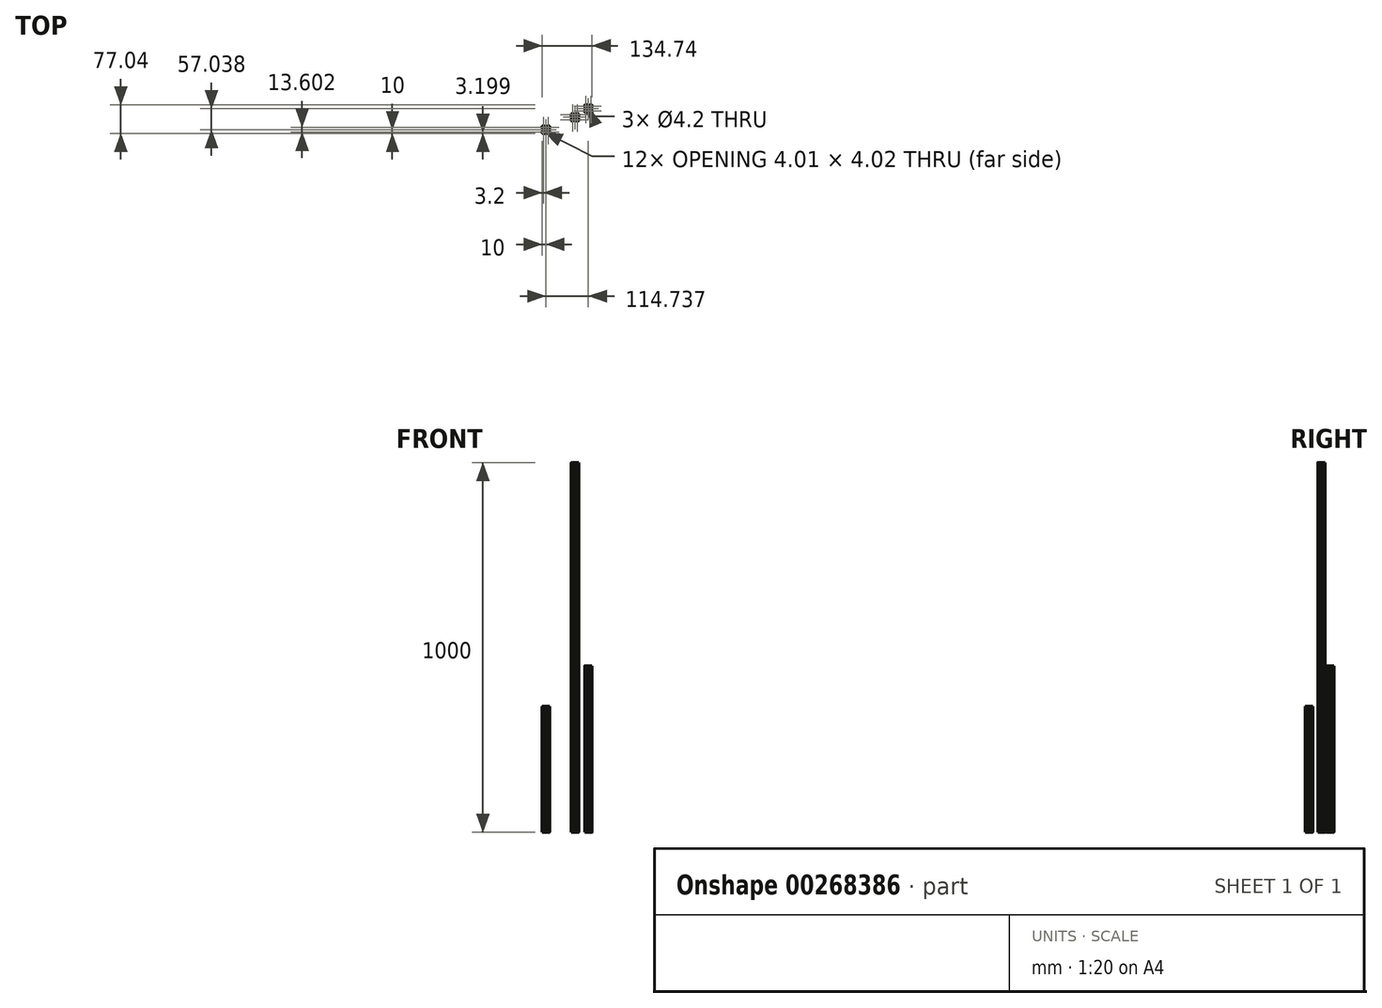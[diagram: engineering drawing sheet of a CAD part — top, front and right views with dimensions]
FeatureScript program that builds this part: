
annotation { "Feature Type Name" : "Feature", "Feature Type Description" : "" }
export const myFeature = defineFeature(function(context is Context, id is Id, definition is map)
    precondition{}
    {
        {
            var Q0;
            Q0=qCreatedBy(makeId("Top.planeOp"),FACE);
            var sketch = newSketch(context, id + "F0", { "sketchPlane" : qUnion([Q0])});
            skLineSegment(sketch, "E0", {"start": v(-9.77, 3.7) * mm, "end": v(-8.49, 2.4) * mm});
            skArc(sketch, "E1", {"start": v(-8.49, 2.4) * mm, "mid": v(-8.27, 2.36) * mm, "end": v(-8.14, 2.54) * mm});
            skLineSegment(sketch, "E2", {"start": v(-8.14, 2.54) * mm, "end": v(-8.14, 3.6) * mm});
            skLineSegment(sketch, "E3", {"start": v(-8.14, 3.6) * mm, "end": v(-5.03, 3.6) * mm});
            skLineSegment(sketch, "E4", {"start": v(-5.03, 3.6) * mm, "end": v(-3.4, 1.97) * mm});
            skLineSegment(sketch, "E5", {"start": v(-3.4, 1.97) * mm, "end": v(-3.4, 0.38) * mm});
            skLineSegment(sketch, "E6", {"start": v(-3.4, 0.38) * mm, "end": v(-3.02, 0) * mm});
            skLineSegment(sketch, "E7", {"start": v(-3.4, -0.38) * mm, "end": v(-3.02, 0) * mm});
            skLineSegment(sketch, "E8", {"start": v(-3.4, -1.97) * mm, "end": v(-3.4, -0.38) * mm});
            skLineSegment(sketch, "E9", {"start": v(-5.03, -3.6) * mm, "end": v(-3.4, -1.97) * mm});
            skLineSegment(sketch, "E10", {"start": v(-8.14, -3.6) * mm, "end": v(-5.03, -3.6) * mm});
            skLineSegment(sketch, "E11", {"start": v(-8.14, -2.54) * mm, "end": v(-8.14, -3.6) * mm});
            skArc(sketch, "E12", {"start": v(-8.49, -2.4) * mm, "mid": v(-8.27, -2.36) * mm, "end": v(-8.14, -2.54) * mm});
            skLineSegment(sketch, "E13", {"start": v(-9.77, -3.7) * mm, "end": v(-8.49, -2.4) * mm});
            skArc(sketch, "E14", {"start": v(-10, -4.25) * mm, "mid": v(-9.94, -3.95) * mm, "end": v(-9.77, -3.7) * mm});
            skLineSegment(sketch, "E15", {"start": v(-10, -8.58) * mm, "end": v(-10, -4.25) * mm});
            skArc(sketch, "E16", {"start": v(-8.6, -10) * mm, "mid": v(-9.57, -9.56) * mm, "end": v(-10, -8.58) * mm});
            skLineSegment(sketch, "E17", {"start": v(-4.04, -10) * mm, "end": v(-8.6, -10) * mm});
            skArc(sketch, "E18", {"start": v(-3.48, -9.77) * mm, "mid": v(-3.74, -9.94) * mm, "end": v(-4.04, -10) * mm});
            skLineSegment(sketch, "E19", {"start": v(-2.37, -8.66) * mm, "end": v(-3.48, -9.77) * mm});
            skArc(sketch, "E20", {"start": v(-2.55, -8.23) * mm, "mid": v(-2.32, -8.39) * mm, "end": v(-2.37, -8.66) * mm});
            skLineSegment(sketch, "E21", {"start": v(-3.6, -8.23) * mm, "end": v(-2.55, -8.23) * mm});
            skLineSegment(sketch, "E22", {"start": v(-3.6, -5.03) * mm, "end": v(-3.6, -8.23) * mm});
            skLineSegment(sketch, "E23", {"start": v(-2, -3.43) * mm, "end": v(-3.6, -5.03) * mm});
            skLineSegment(sketch, "E24", {"start": v(-0.3, -3.43) * mm, "end": v(-2, -3.43) * mm});
            skLineSegment(sketch, "E25", {"start": v(0, -3.18) * mm, "end": v(-0.3, -3.43) * mm});
            skLineSegment(sketch, "E26", {"start": v(0, -3.18) * mm, "end": v(0.3, -3.43) * mm});
            skLineSegment(sketch, "E27", {"start": v(0.3, -3.43) * mm, "end": v(2, -3.43) * mm});
            skLineSegment(sketch, "E28", {"start": v(2, -3.43) * mm, "end": v(3.6, -5.03) * mm});
            skLineSegment(sketch, "E29", {"start": v(3.6, -5.03) * mm, "end": v(3.6, -8.23) * mm});
            skLineSegment(sketch, "E30", {"start": v(3.6, -8.23) * mm, "end": v(2.55, -8.23) * mm});
            skArc(sketch, "E31", {"start": v(2.55, -8.23) * mm, "mid": v(2.32, -8.39) * mm, "end": v(2.37, -8.66) * mm});
            skLineSegment(sketch, "E32", {"start": v(2.37, -8.66) * mm, "end": v(3.48, -9.77) * mm});
            skArc(sketch, "E33", {"start": v(3.48, -9.77) * mm, "mid": v(3.74, -9.94) * mm, "end": v(4.04, -10) * mm});
            skLineSegment(sketch, "E34", {"start": v(4.04, -10) * mm, "end": v(8.6, -10) * mm});
            skArc(sketch, "E35", {"start": v(8.6, -10) * mm, "mid": v(9.57, -9.56) * mm, "end": v(10, -8.58) * mm});
            skLineSegment(sketch, "E36", {"start": v(10, -8.58) * mm, "end": v(10, -4.25) * mm});
            skArc(sketch, "E37", {"start": v(10, -4.25) * mm, "mid": v(9.94, -3.95) * mm, "end": v(9.77, -3.7) * mm});
            skLineSegment(sketch, "E38", {"start": v(9.77, -3.7) * mm, "end": v(8.49, -2.4) * mm});
            skArc(sketch, "E39", {"start": v(8.49, -2.4) * mm, "mid": v(8.27, -2.36) * mm, "end": v(8.14, -2.54) * mm});
            skLineSegment(sketch, "E40", {"start": v(8.14, -2.54) * mm, "end": v(8.14, -3.6) * mm});
            skLineSegment(sketch, "E41", {"start": v(8.14, -3.6) * mm, "end": v(5.03, -3.6) * mm});
            skLineSegment(sketch, "E42", {"start": v(5.03, -3.6) * mm, "end": v(3.4, -1.97) * mm});
            skLineSegment(sketch, "E43", {"start": v(3.4, -1.97) * mm, "end": v(3.4, -0.38) * mm});
            skLineSegment(sketch, "E44", {"start": v(3.4, -0.38) * mm, "end": v(3.02, 0) * mm});
            skLineSegment(sketch, "E45", {"start": v(3.4, 0.38) * mm, "end": v(3.02, 0) * mm});
            skLineSegment(sketch, "E46", {"start": v(3.4, 1.97) * mm, "end": v(3.4, 0.38) * mm});
            skLineSegment(sketch, "E47", {"start": v(5.03, 3.6) * mm, "end": v(3.4, 1.97) * mm});
            skLineSegment(sketch, "E48", {"start": v(8.14, 3.6) * mm, "end": v(5.03, 3.6) * mm});
            skLineSegment(sketch, "E49", {"start": v(8.14, 2.54) * mm, "end": v(8.14, 3.6) * mm});
            skArc(sketch, "E50", {"start": v(8.49, 2.4) * mm, "mid": v(8.27, 2.36) * mm, "end": v(8.14, 2.54) * mm});
            skLineSegment(sketch, "E51", {"start": v(9.77, 3.7) * mm, "end": v(8.49, 2.4) * mm});
            skArc(sketch, "E52", {"start": v(10, 4.25) * mm, "mid": v(9.94, 3.95) * mm, "end": v(9.77, 3.7) * mm});
            skLineSegment(sketch, "E53", {"start": v(10, 8.58) * mm, "end": v(10, 4.25) * mm});
            skArc(sketch, "E54", {"start": v(8.6, 10) * mm, "mid": v(9.57, 9.56) * mm, "end": v(10, 8.58) * mm});
            skLineSegment(sketch, "E55", {"start": v(4.04, 10) * mm, "end": v(8.6, 10) * mm});
            skArc(sketch, "E56", {"start": v(3.48, 9.77) * mm, "mid": v(3.74, 9.94) * mm, "end": v(4.04, 10) * mm});
            skLineSegment(sketch, "E57", {"start": v(2.37, 8.66) * mm, "end": v(3.48, 9.77) * mm});
            skArc(sketch, "E58", {"start": v(2.55, 8.23) * mm, "mid": v(2.32, 8.39) * mm, "end": v(2.37, 8.66) * mm});
            skLineSegment(sketch, "E59", {"start": v(3.6, 8.23) * mm, "end": v(2.55, 8.23) * mm});
            skLineSegment(sketch, "E60", {"start": v(3.6, 5.03) * mm, "end": v(3.6, 8.23) * mm});
            skLineSegment(sketch, "E61", {"start": v(2, 3.43) * mm, "end": v(3.6, 5.03) * mm});
            skLineSegment(sketch, "E62", {"start": v(0.3, 3.43) * mm, "end": v(2, 3.43) * mm});
            skLineSegment(sketch, "E63", {"start": v(0, 3.18) * mm, "end": v(0.3, 3.43) * mm});
            skLineSegment(sketch, "E64", {"start": v(0, 3.18) * mm, "end": v(-0.3, 3.43) * mm});
            skLineSegment(sketch, "E65", {"start": v(-0.3, 3.43) * mm, "end": v(-2, 3.43) * mm});
            skLineSegment(sketch, "E66", {"start": v(-2, 3.43) * mm, "end": v(-3.6, 5.03) * mm});
            skLineSegment(sketch, "E67", {"start": v(-3.6, 5.03) * mm, "end": v(-3.6, 8.23) * mm});
            skLineSegment(sketch, "E68", {"start": v(-3.6, 8.23) * mm, "end": v(-2.55, 8.23) * mm});
            skArc(sketch, "E69", {"start": v(-2.55, 8.23) * mm, "mid": v(-2.32, 8.39) * mm, "end": v(-2.37, 8.66) * mm});
            skLineSegment(sketch, "E70", {"start": v(-2.37, 8.66) * mm, "end": v(-3.48, 9.77) * mm});
            skArc(sketch, "E71", {"start": v(-3.48, 9.77) * mm, "mid": v(-3.74, 9.94) * mm, "end": v(-4.04, 10) * mm});
            skLineSegment(sketch, "E72", {"start": v(-4.04, 10) * mm, "end": v(-8.6, 10) * mm});
            skArc(sketch, "E73", {"start": v(-8.6, 10) * mm, "mid": v(-9.57, 9.56) * mm, "end": v(-10, 8.58) * mm});
            skLineSegment(sketch, "E74", {"start": v(-10, 8.58) * mm, "end": v(-10, 4.25) * mm});
            skArc(sketch, "E75", {"start": v(-10, 4.25) * mm, "mid": v(-9.94, 3.95) * mm, "end": v(-9.77, 3.7) * mm});
            skLineSegment(sketch, "E76", {"start": v(-8.8, -5.38) * mm, "end": v(-8.8, -8.38) * mm});
            skArc(sketch, "E77", {"start": v(-8.8, -5.38) * mm, "mid": v(-8.72, -5) * mm, "end": v(-8.39, -4.8) * mm});
            skLineSegment(sketch, "E78", {"start": v(-5.39, -4.8) * mm, "end": v(-8.39, -4.8) * mm});
            skArc(sketch, "E79", {"start": v(-5.39, -4.8) * mm, "mid": v(-4.94, -4.93) * mm, "end": v(-4.8, -5.38) * mm});
            skLineSegment(sketch, "E80", {"start": v(-4.8, -8.38) * mm, "end": v(-4.8, -5.38) * mm});
            skArc(sketch, "E81", {"start": v(-4.8, -8.38) * mm, "mid": v(-5, -8.72) * mm, "end": v(-5.4, -8.8) * mm});
            skLineSegment(sketch, "E82", {"start": v(-8.4, -8.8) * mm, "end": v(-5.4, -8.8) * mm});
            skArc(sketch, "E83", {"start": v(-8.4, -8.8) * mm, "mid": v(-8.67, -8.65) * mm, "end": v(-8.8, -8.38) * mm});
            skLineSegment(sketch, "E84", {"start": v(8.8, 5.38) * mm, "end": v(8.8, 8.38) * mm});
            skArc(sketch, "E85", {"start": v(8.8, 5.38) * mm, "mid": v(8.72, 5) * mm, "end": v(8.39, 4.8) * mm});
            skLineSegment(sketch, "E86", {"start": v(5.4, 4.93) * mm, "end": v(5.39, 4.8) * mm});
            skArc(sketch, "E87", {"start": v(5.39, 4.8) * mm, "mid": v(4.94, 4.93) * mm, "end": v(4.8, 5.38) * mm});
            skLineSegment(sketch, "E88", {"start": v(4.8, 8.38) * mm, "end": v(4.8, 5.38) * mm});
            skArc(sketch, "E89", {"start": v(4.8, 8.38) * mm, "mid": v(5, 8.72) * mm, "end": v(5.4, 8.8) * mm});
            skLineSegment(sketch, "E90", {"start": v(8.4, 8.8) * mm, "end": v(5.4, 8.8) * mm});
            skArc(sketch, "E91", {"start": v(8.4, 8.8) * mm, "mid": v(8.67, 8.65) * mm, "end": v(8.8, 8.38) * mm});
            skArc(sketch, "E92", {"start": v(5.39, -4.8) * mm, "mid": v(4.94, -4.93) * mm, "end": v(4.8, -5.38) * mm});
            skLineSegment(sketch, "E93", {"start": v(5.39, -4.8) * mm, "end": v(8.39, -4.8) * mm});
            skArc(sketch, "E94", {"start": v(8.8, -5.38) * mm, "mid": v(8.72, -5) * mm, "end": v(8.39, -4.8) * mm});
            skLineSegment(sketch, "E95", {"start": v(8.8, -5.38) * mm, "end": v(8.8, -8.38) * mm});
            skArc(sketch, "E96", {"start": v(8.4, -8.8) * mm, "mid": v(8.67, -8.65) * mm, "end": v(8.8, -8.38) * mm});
            skLineSegment(sketch, "E97", {"start": v(8.4, -8.8) * mm, "end": v(5.4, -8.8) * mm});
            skArc(sketch, "E98", {"start": v(4.8, -8.38) * mm, "mid": v(5, -8.72) * mm, "end": v(5.4, -8.8) * mm});
            skLineSegment(sketch, "E99", {"start": v(4.8, -8.38) * mm, "end": v(4.8, -5.38) * mm});
            skCircle(sketch, "E100", {"center": v(0, 0) * mm, "radius": 2.1 * mm});
            skArc(sketch, "E101", {"start": v(-5.39, 4.8) * mm, "mid": v(-4.94, 4.93) * mm, "end": v(-4.8, 5.38) * mm});
            skLineSegment(sketch, "E102", {"start": v(-5.39, 4.8) * mm, "end": v(-8.39, 4.8) * mm});
            skArc(sketch, "E103", {"start": v(-8.8, 5.38) * mm, "mid": v(-8.72, 5) * mm, "end": v(-8.39, 4.8) * mm});
            skLineSegment(sketch, "E104", {"start": v(-8.8, 5.38) * mm, "end": v(-8.8, 8.38) * mm});
            skArc(sketch, "E105", {"start": v(-8.4, 8.8) * mm, "mid": v(-8.67, 8.65) * mm, "end": v(-8.8, 8.38) * mm});
            skLineSegment(sketch, "E106", {"start": v(-8.4, 8.8) * mm, "end": v(-5.4, 8.8) * mm});
            skArc(sketch, "E107", {"start": v(-4.8, 8.38) * mm, "mid": v(-5, 8.72) * mm, "end": v(-5.4, 8.8) * mm});
            skLineSegment(sketch, "E108", {"start": v(-4.8, 8.38) * mm, "end": v(-4.8, 5.38) * mm});
            skLineSegment(sketch, "E109", {"start": v(5.39, 4.8) * mm, "end": v(8.39, 4.8) * mm});
            skLineSegment(sketch, "E110", {"start": v(-0.3, -3.43) * mm, "end": v(0.56, -10) * mm, "construction": true});
            skLineSegment(sketch, "E111", {"start": v(104.97, 60.73) * mm, "end": v(106.25, 59.45) * mm});
            skArc(sketch, "E112", {"start": v(106.25, 59.45) * mm, "mid": v(106.46, 59.4) * mm, "end": v(106.6, 59.58) * mm});
            skLineSegment(sketch, "E113", {"start": v(106.6, 59.58) * mm, "end": v(106.6, 60.64) * mm});
            skLineSegment(sketch, "E114", {"start": v(106.6, 60.64) * mm, "end": v(109.7, 60.64) * mm});
            skLineSegment(sketch, "E115", {"start": v(109.7, 60.64) * mm, "end": v(111.34, 59) * mm});
            skLineSegment(sketch, "E116", {"start": v(111.34, 59) * mm, "end": v(111.34, 57.42) * mm});
            skLineSegment(sketch, "E117", {"start": v(111.34, 57.42) * mm, "end": v(111.72, 57.04) * mm});
            skLineSegment(sketch, "E118", {"start": v(111.34, 56.66) * mm, "end": v(111.72, 57.04) * mm});
            skLineSegment(sketch, "E119", {"start": v(111.34, 55.07) * mm, "end": v(111.34, 56.66) * mm});
            skLineSegment(sketch, "E120", {"start": v(109.7, 53.44) * mm, "end": v(111.34, 55.07) * mm});
            skLineSegment(sketch, "E121", {"start": v(106.6, 53.44) * mm, "end": v(109.7, 53.44) * mm});
            skLineSegment(sketch, "E122", {"start": v(106.6, 54.5) * mm, "end": v(106.6, 53.44) * mm});
            skArc(sketch, "E123", {"start": v(106.25, 54.63) * mm, "mid": v(106.46, 54.67) * mm, "end": v(106.6, 54.5) * mm});
            skLineSegment(sketch, "E124", {"start": v(104.97, 53.35) * mm, "end": v(106.25, 54.63) * mm});
            skArc(sketch, "E125", {"start": v(104.74, 52.79) * mm, "mid": v(104.8, 53.1) * mm, "end": v(104.97, 53.35) * mm});
            skLineSegment(sketch, "E126", {"start": v(104.74, 48.46) * mm, "end": v(104.74, 52.79) * mm});
            skArc(sketch, "E127", {"start": v(106.14, 47.04) * mm, "mid": v(105.17, 47.48) * mm, "end": v(104.74, 48.46) * mm});
            skLineSegment(sketch, "E128", {"start": v(110.7, 47.04) * mm, "end": v(106.14, 47.04) * mm});
            skArc(sketch, "E129", {"start": v(111.26, 47.27) * mm, "mid": v(111, 47.1) * mm, "end": v(110.7, 47.04) * mm});
            skLineSegment(sketch, "E130", {"start": v(112.36, 48.38) * mm, "end": v(111.26, 47.27) * mm});
            skArc(sketch, "E131", {"start": v(112.19, 48.8) * mm, "mid": v(112.42, 48.65) * mm, "end": v(112.36, 48.38) * mm});
            skLineSegment(sketch, "E132", {"start": v(111.14, 48.8) * mm, "end": v(112.19, 48.8) * mm});
            skLineSegment(sketch, "E133", {"start": v(111.14, 52) * mm, "end": v(111.14, 48.8) * mm});
            skLineSegment(sketch, "E134", {"start": v(112.73, 53.6) * mm, "end": v(111.14, 52) * mm});
            skLineSegment(sketch, "E135", {"start": v(114.44, 53.6) * mm, "end": v(112.73, 53.6) * mm});
            skLineSegment(sketch, "E136", {"start": v(114.74, 53.86) * mm, "end": v(114.44, 53.6) * mm});
            skLineSegment(sketch, "E137", {"start": v(114.74, 53.86) * mm, "end": v(115.04, 53.6) * mm});
            skLineSegment(sketch, "E138", {"start": v(115.04, 53.6) * mm, "end": v(116.74, 53.6) * mm});
            skLineSegment(sketch, "E139", {"start": v(116.74, 53.6) * mm, "end": v(118.34, 52) * mm});
            skLineSegment(sketch, "E140", {"start": v(118.34, 52) * mm, "end": v(118.34, 48.8) * mm});
            skLineSegment(sketch, "E141", {"start": v(118.34, 48.8) * mm, "end": v(117.29, 48.8) * mm});
            skArc(sketch, "E142", {"start": v(117.29, 48.8) * mm, "mid": v(117.06, 48.65) * mm, "end": v(117.11, 48.38) * mm});
            skLineSegment(sketch, "E143", {"start": v(117.11, 48.38) * mm, "end": v(118.21, 47.27) * mm});
            skArc(sketch, "E144", {"start": v(118.21, 47.27) * mm, "mid": v(118.47, 47.1) * mm, "end": v(118.78, 47.04) * mm});
            skLineSegment(sketch, "E145", {"start": v(118.78, 47.04) * mm, "end": v(123.34, 47.04) * mm});
            skArc(sketch, "E146", {"start": v(123.34, 47.04) * mm, "mid": v(124.3, 47.48) * mm, "end": v(124.74, 48.46) * mm});
            skLineSegment(sketch, "E147", {"start": v(124.74, 48.46) * mm, "end": v(124.74, 52.79) * mm});
            skArc(sketch, "E148", {"start": v(124.74, 52.79) * mm, "mid": v(124.68, 53.1) * mm, "end": v(124.5, 53.35) * mm});
            skLineSegment(sketch, "E149", {"start": v(124.5, 53.35) * mm, "end": v(123.22, 54.63) * mm});
            skArc(sketch, "E150", {"start": v(123.22, 54.63) * mm, "mid": v(123, 54.67) * mm, "end": v(122.88, 54.5) * mm});
            skLineSegment(sketch, "E151", {"start": v(122.88, 54.5) * mm, "end": v(122.88, 53.44) * mm});
            skLineSegment(sketch, "E152", {"start": v(122.88, 53.44) * mm, "end": v(119.77, 53.44) * mm});
            skLineSegment(sketch, "E153", {"start": v(119.77, 53.44) * mm, "end": v(118.14, 55.07) * mm});
            skLineSegment(sketch, "E154", {"start": v(118.14, 55.07) * mm, "end": v(118.14, 56.66) * mm});
            skLineSegment(sketch, "E155", {"start": v(118.14, 56.66) * mm, "end": v(117.76, 57.04) * mm});
            skLineSegment(sketch, "E156", {"start": v(118.14, 57.42) * mm, "end": v(117.76, 57.04) * mm});
            skLineSegment(sketch, "E157", {"start": v(118.14, 59) * mm, "end": v(118.14, 57.42) * mm});
            skLineSegment(sketch, "E158", {"start": v(119.77, 60.64) * mm, "end": v(118.14, 59) * mm});
            skLineSegment(sketch, "E159", {"start": v(122.88, 60.64) * mm, "end": v(119.77, 60.64) * mm});
            skLineSegment(sketch, "E160", {"start": v(122.88, 59.58) * mm, "end": v(122.88, 60.64) * mm});
            skArc(sketch, "E161", {"start": v(123.22, 59.45) * mm, "mid": v(123, 59.4) * mm, "end": v(122.88, 59.58) * mm});
            skLineSegment(sketch, "E162", {"start": v(124.5, 60.73) * mm, "end": v(123.22, 59.45) * mm});
            skArc(sketch, "E163", {"start": v(124.74, 61.29) * mm, "mid": v(124.68, 60.98) * mm, "end": v(124.5, 60.73) * mm});
            skLineSegment(sketch, "E164", {"start": v(124.74, 65.62) * mm, "end": v(124.74, 61.29) * mm});
            skArc(sketch, "E165", {"start": v(123.34, 67.04) * mm, "mid": v(124.3, 66.6) * mm, "end": v(124.74, 65.62) * mm});
            skLineSegment(sketch, "E166", {"start": v(118.78, 67.04) * mm, "end": v(123.34, 67.04) * mm});
            skArc(sketch, "E167", {"start": v(118.21, 66.8) * mm, "mid": v(118.47, 66.98) * mm, "end": v(118.78, 67.04) * mm});
            skLineSegment(sketch, "E168", {"start": v(117.11, 65.7) * mm, "end": v(118.21, 66.8) * mm});
            skArc(sketch, "E169", {"start": v(117.29, 65.27) * mm, "mid": v(117.06, 65.43) * mm, "end": v(117.11, 65.7) * mm});
            skLineSegment(sketch, "E170", {"start": v(118.34, 65.27) * mm, "end": v(117.29, 65.27) * mm});
            skLineSegment(sketch, "E171", {"start": v(118.34, 62.07) * mm, "end": v(118.34, 65.27) * mm});
            skLineSegment(sketch, "E172", {"start": v(116.74, 60.47) * mm, "end": v(118.34, 62.07) * mm});
            skLineSegment(sketch, "E173", {"start": v(115.04, 60.47) * mm, "end": v(116.74, 60.47) * mm});
            skLineSegment(sketch, "E174", {"start": v(114.74, 60.21) * mm, "end": v(115.04, 60.47) * mm});
            skLineSegment(sketch, "E175", {"start": v(114.74, 60.21) * mm, "end": v(114.44, 60.47) * mm});
            skLineSegment(sketch, "E176", {"start": v(114.44, 60.47) * mm, "end": v(112.73, 60.47) * mm});
            skLineSegment(sketch, "E177", {"start": v(112.73, 60.47) * mm, "end": v(111.14, 62.07) * mm});
            skLineSegment(sketch, "E178", {"start": v(111.14, 62.07) * mm, "end": v(111.14, 65.27) * mm});
            skLineSegment(sketch, "E179", {"start": v(111.14, 65.27) * mm, "end": v(112.19, 65.27) * mm});
            skArc(sketch, "E180", {"start": v(112.19, 65.27) * mm, "mid": v(112.42, 65.43) * mm, "end": v(112.36, 65.7) * mm});
            skLineSegment(sketch, "E181", {"start": v(112.36, 65.7) * mm, "end": v(111.26, 66.8) * mm});
            skArc(sketch, "E182", {"start": v(111.26, 66.8) * mm, "mid": v(111, 66.98) * mm, "end": v(110.7, 67.04) * mm});
            skLineSegment(sketch, "E183", {"start": v(110.7, 67.04) * mm, "end": v(106.14, 67.04) * mm});
            skArc(sketch, "E184", {"start": v(106.14, 67.04) * mm, "mid": v(105.17, 66.6) * mm, "end": v(104.74, 65.62) * mm});
            skLineSegment(sketch, "E185", {"start": v(104.74, 65.62) * mm, "end": v(104.74, 61.29) * mm});
            skArc(sketch, "E186", {"start": v(104.74, 61.29) * mm, "mid": v(104.8, 60.98) * mm, "end": v(104.97, 60.73) * mm});
            skLineSegment(sketch, "E187", {"start": v(105.94, 51.66) * mm, "end": v(105.94, 48.66) * mm});
            skArc(sketch, "E188", {"start": v(105.94, 51.66) * mm, "mid": v(106.02, 52.03) * mm, "end": v(106.35, 52.24) * mm});
            skLineSegment(sketch, "E189", {"start": v(109.35, 52.24) * mm, "end": v(106.35, 52.24) * mm});
            skArc(sketch, "E190", {"start": v(109.35, 52.24) * mm, "mid": v(109.8, 52.1) * mm, "end": v(109.94, 51.66) * mm});
            skLineSegment(sketch, "E191", {"start": v(109.94, 48.66) * mm, "end": v(109.94, 51.66) * mm});
            skArc(sketch, "E192", {"start": v(109.94, 48.66) * mm, "mid": v(109.73, 48.32) * mm, "end": v(109.34, 48.24) * mm});
            skLineSegment(sketch, "E193", {"start": v(106.34, 48.24) * mm, "end": v(109.34, 48.24) * mm});
            skArc(sketch, "E194", {"start": v(106.34, 48.24) * mm, "mid": v(106.07, 48.38) * mm, "end": v(105.94, 48.66) * mm});
            skLineSegment(sketch, "E195", {"start": v(123.54, 62.42) * mm, "end": v(123.54, 65.42) * mm});
            skArc(sketch, "E196", {"start": v(123.54, 62.42) * mm, "mid": v(123.45, 62.04) * mm, "end": v(123.13, 61.84) * mm});
            skLineSegment(sketch, "E197", {"start": v(120.13, 61.97) * mm, "end": v(120.13, 61.84) * mm});
            skArc(sketch, "E198", {"start": v(120.13, 61.84) * mm, "mid": v(119.68, 61.97) * mm, "end": v(119.54, 62.42) * mm});
            skLineSegment(sketch, "E199", {"start": v(119.54, 65.42) * mm, "end": v(119.54, 62.42) * mm});
            skArc(sketch, "E200", {"start": v(119.54, 65.42) * mm, "mid": v(119.75, 65.76) * mm, "end": v(120.14, 65.84) * mm});
            skLineSegment(sketch, "E201", {"start": v(123.14, 65.84) * mm, "end": v(120.14, 65.84) * mm});
            skArc(sketch, "E202", {"start": v(123.14, 65.84) * mm, "mid": v(123.4, 65.7) * mm, "end": v(123.54, 65.42) * mm});
            skArc(sketch, "E203", {"start": v(120.13, 52.24) * mm, "mid": v(119.68, 52.1) * mm, "end": v(119.54, 51.66) * mm});
            skLineSegment(sketch, "E204", {"start": v(120.13, 52.24) * mm, "end": v(123.13, 52.24) * mm});
            skArc(sketch, "E205", {"start": v(123.54, 51.66) * mm, "mid": v(123.45, 52.03) * mm, "end": v(123.13, 52.24) * mm});
            skLineSegment(sketch, "E206", {"start": v(123.54, 51.66) * mm, "end": v(123.54, 48.66) * mm});
            skArc(sketch, "E207", {"start": v(123.14, 48.24) * mm, "mid": v(123.4, 48.38) * mm, "end": v(123.54, 48.66) * mm});
            skLineSegment(sketch, "E208", {"start": v(123.14, 48.24) * mm, "end": v(120.14, 48.24) * mm});
            skArc(sketch, "E209", {"start": v(119.54, 48.66) * mm, "mid": v(119.75, 48.32) * mm, "end": v(120.14, 48.24) * mm});
            skLineSegment(sketch, "E210", {"start": v(119.54, 48.66) * mm, "end": v(119.54, 51.66) * mm});
            skCircle(sketch, "E211", {"center": v(114.74, 57.04) * mm, "radius": 2.1 * mm});
            skArc(sketch, "E212", {"start": v(109.35, 61.84) * mm, "mid": v(109.8, 61.97) * mm, "end": v(109.94, 62.42) * mm});
            skLineSegment(sketch, "E213", {"start": v(109.35, 61.84) * mm, "end": v(106.35, 61.84) * mm});
            skArc(sketch, "E214", {"start": v(105.94, 62.42) * mm, "mid": v(106.02, 62.04) * mm, "end": v(106.35, 61.84) * mm});
            skLineSegment(sketch, "E215", {"start": v(105.94, 62.42) * mm, "end": v(105.94, 65.42) * mm});
            skArc(sketch, "E216", {"start": v(106.34, 65.84) * mm, "mid": v(106.07, 65.7) * mm, "end": v(105.94, 65.42) * mm});
            skLineSegment(sketch, "E217", {"start": v(106.34, 65.84) * mm, "end": v(109.34, 65.84) * mm});
            skArc(sketch, "E218", {"start": v(109.94, 65.42) * mm, "mid": v(109.73, 65.76) * mm, "end": v(109.34, 65.84) * mm});
            skLineSegment(sketch, "E219", {"start": v(109.94, 65.42) * mm, "end": v(109.94, 62.42) * mm});
            skLineSegment(sketch, "E220", {"start": v(120.13, 61.84) * mm, "end": v(123.13, 61.84) * mm});
            skLineSegment(sketch, "E221", {"start": v(114.44, 53.6) * mm, "end": v(115.3, 47.04) * mm, "construction": true});
            skLineSegment(sketch, "E222", {"start": v(68.81, 37.37) * mm, "end": v(70.1, 36.09) * mm});
            skArc(sketch, "E223", {"start": v(70.1, 36.09) * mm, "mid": v(70.3, 36.04) * mm, "end": v(70.44, 36.22) * mm});
            skLineSegment(sketch, "E224", {"start": v(70.44, 36.22) * mm, "end": v(70.44, 37.28) * mm});
            skLineSegment(sketch, "E225", {"start": v(70.44, 37.28) * mm, "end": v(73.55, 37.28) * mm});
            skLineSegment(sketch, "E226", {"start": v(73.55, 37.28) * mm, "end": v(75.18, 35.65) * mm});
            skLineSegment(sketch, "E227", {"start": v(75.18, 35.65) * mm, "end": v(75.18, 34.06) * mm});
            skLineSegment(sketch, "E228", {"start": v(75.18, 34.06) * mm, "end": v(75.56, 33.68) * mm});
            skLineSegment(sketch, "E229", {"start": v(75.18, 33.3) * mm, "end": v(75.56, 33.68) * mm});
            skLineSegment(sketch, "E230", {"start": v(75.18, 31.71) * mm, "end": v(75.18, 33.3) * mm});
            skLineSegment(sketch, "E231", {"start": v(73.55, 30.08) * mm, "end": v(75.18, 31.71) * mm});
            skLineSegment(sketch, "E232", {"start": v(70.44, 30.08) * mm, "end": v(73.55, 30.08) * mm});
            skLineSegment(sketch, "E233", {"start": v(70.44, 31.14) * mm, "end": v(70.44, 30.08) * mm});
            skArc(sketch, "E234", {"start": v(70.1, 31.27) * mm, "mid": v(70.3, 31.32) * mm, "end": v(70.44, 31.14) * mm});
            skLineSegment(sketch, "E235", {"start": v(68.81, 29.99) * mm, "end": v(70.1, 31.27) * mm});
            skArc(sketch, "E236", {"start": v(68.58, 29.43) * mm, "mid": v(68.64, 29.73) * mm, "end": v(68.81, 29.99) * mm});
            skLineSegment(sketch, "E237", {"start": v(68.58, 25.1) * mm, "end": v(68.58, 29.43) * mm});
            skArc(sketch, "E238", {"start": v(69.98, 23.68) * mm, "mid": v(69.01, 24.12) * mm, "end": v(68.58, 25.1) * mm});
            skLineSegment(sketch, "E239", {"start": v(74.54, 23.68) * mm, "end": v(69.98, 23.68) * mm});
            skArc(sketch, "E240", {"start": v(75.1, 23.91) * mm, "mid": v(74.84, 23.74) * mm, "end": v(74.54, 23.68) * mm});
            skLineSegment(sketch, "E241", {"start": v(76.2, 25.02) * mm, "end": v(75.1, 23.91) * mm});
            skArc(sketch, "E242", {"start": v(76.03, 25.44) * mm, "mid": v(76.26, 25.29) * mm, "end": v(76.2, 25.02) * mm});
            skLineSegment(sketch, "E243", {"start": v(74.98, 25.44) * mm, "end": v(76.03, 25.44) * mm});
            skLineSegment(sketch, "E244", {"start": v(74.98, 28.64) * mm, "end": v(74.98, 25.44) * mm});
            skLineSegment(sketch, "E245", {"start": v(76.57, 30.24) * mm, "end": v(74.98, 28.64) * mm});
            skLineSegment(sketch, "E246", {"start": v(78.28, 30.24) * mm, "end": v(76.57, 30.24) * mm});
            skLineSegment(sketch, "E247", {"start": v(78.58, 30.5) * mm, "end": v(78.28, 30.24) * mm});
            skLineSegment(sketch, "E248", {"start": v(78.58, 30.5) * mm, "end": v(78.88, 30.24) * mm});
            skLineSegment(sketch, "E249", {"start": v(78.88, 30.24) * mm, "end": v(80.59, 30.24) * mm});
            skLineSegment(sketch, "E250", {"start": v(80.59, 30.24) * mm, "end": v(82.18, 28.64) * mm});
            skLineSegment(sketch, "E251", {"start": v(82.18, 28.64) * mm, "end": v(82.18, 25.44) * mm});
            skLineSegment(sketch, "E252", {"start": v(82.18, 25.44) * mm, "end": v(81.13, 25.44) * mm});
            skArc(sketch, "E253", {"start": v(81.13, 25.44) * mm, "mid": v(80.9, 25.29) * mm, "end": v(80.95, 25.02) * mm});
            skLineSegment(sketch, "E254", {"start": v(80.95, 25.02) * mm, "end": v(82.06, 23.91) * mm});
            skArc(sketch, "E255", {"start": v(82.06, 23.91) * mm, "mid": v(82.32, 23.74) * mm, "end": v(82.62, 23.68) * mm});
            skLineSegment(sketch, "E256", {"start": v(82.62, 23.68) * mm, "end": v(87.18, 23.68) * mm});
            skArc(sketch, "E257", {"start": v(87.18, 23.68) * mm, "mid": v(88.15, 24.12) * mm, "end": v(88.58, 25.1) * mm});
            skLineSegment(sketch, "E258", {"start": v(88.58, 25.1) * mm, "end": v(88.58, 29.43) * mm});
            skArc(sketch, "E259", {"start": v(88.58, 29.43) * mm, "mid": v(88.52, 29.73) * mm, "end": v(88.35, 29.99) * mm});
            skLineSegment(sketch, "E260", {"start": v(88.35, 29.99) * mm, "end": v(87.07, 31.27) * mm});
            skArc(sketch, "E261", {"start": v(87.07, 31.27) * mm, "mid": v(86.85, 31.32) * mm, "end": v(86.73, 31.14) * mm});
            skLineSegment(sketch, "E262", {"start": v(86.73, 31.14) * mm, "end": v(86.73, 30.08) * mm});
            skLineSegment(sketch, "E263", {"start": v(86.73, 30.08) * mm, "end": v(83.6, 30.08) * mm});
            skLineSegment(sketch, "E264", {"start": v(83.6, 30.08) * mm, "end": v(81.98, 31.71) * mm});
            skLineSegment(sketch, "E265", {"start": v(81.98, 31.71) * mm, "end": v(81.98, 33.3) * mm});
            skLineSegment(sketch, "E266", {"start": v(81.98, 33.3) * mm, "end": v(81.6, 33.68) * mm});
            skLineSegment(sketch, "E267", {"start": v(81.98, 34.06) * mm, "end": v(81.6, 33.68) * mm});
            skLineSegment(sketch, "E268", {"start": v(81.98, 35.65) * mm, "end": v(81.98, 34.06) * mm});
            skLineSegment(sketch, "E269", {"start": v(83.6, 37.28) * mm, "end": v(81.98, 35.65) * mm});
            skLineSegment(sketch, "E270", {"start": v(86.73, 37.28) * mm, "end": v(83.6, 37.28) * mm});
            skLineSegment(sketch, "E271", {"start": v(86.73, 36.22) * mm, "end": v(86.73, 37.28) * mm});
            skArc(sketch, "E272", {"start": v(87.07, 36.09) * mm, "mid": v(86.85, 36.04) * mm, "end": v(86.73, 36.22) * mm});
            skLineSegment(sketch, "E273", {"start": v(88.35, 37.37) * mm, "end": v(87.07, 36.09) * mm});
            skArc(sketch, "E274", {"start": v(88.58, 37.93) * mm, "mid": v(88.52, 37.63) * mm, "end": v(88.35, 37.37) * mm});
            skLineSegment(sketch, "E275", {"start": v(88.58, 42.26) * mm, "end": v(88.58, 37.93) * mm});
            skArc(sketch, "E276", {"start": v(87.18, 43.68) * mm, "mid": v(88.15, 43.24) * mm, "end": v(88.58, 42.26) * mm});
            skLineSegment(sketch, "E277", {"start": v(82.62, 43.68) * mm, "end": v(87.18, 43.68) * mm});
            skArc(sketch, "E278", {"start": v(82.06, 43.44) * mm, "mid": v(82.32, 43.62) * mm, "end": v(82.62, 43.68) * mm});
            skLineSegment(sketch, "E279", {"start": v(80.95, 42.34) * mm, "end": v(82.06, 43.44) * mm});
            skArc(sketch, "E280", {"start": v(81.13, 41.91) * mm, "mid": v(80.9, 42.07) * mm, "end": v(80.95, 42.34) * mm});
            skLineSegment(sketch, "E281", {"start": v(82.18, 41.91) * mm, "end": v(81.13, 41.91) * mm});
            skLineSegment(sketch, "E282", {"start": v(82.18, 38.71) * mm, "end": v(82.18, 41.91) * mm});
            skLineSegment(sketch, "E283", {"start": v(80.59, 37.11) * mm, "end": v(82.18, 38.71) * mm});
            skLineSegment(sketch, "E284", {"start": v(78.88, 37.11) * mm, "end": v(80.59, 37.11) * mm});
            skLineSegment(sketch, "E285", {"start": v(78.58, 36.85) * mm, "end": v(78.88, 37.11) * mm});
            skLineSegment(sketch, "E286", {"start": v(78.58, 36.85) * mm, "end": v(78.28, 37.11) * mm});
            skLineSegment(sketch, "E287", {"start": v(78.28, 37.11) * mm, "end": v(76.57, 37.11) * mm});
            skLineSegment(sketch, "E288", {"start": v(76.57, 37.11) * mm, "end": v(74.98, 38.71) * mm});
            skLineSegment(sketch, "E289", {"start": v(74.98, 38.71) * mm, "end": v(74.98, 41.91) * mm});
            skLineSegment(sketch, "E290", {"start": v(74.98, 41.91) * mm, "end": v(76.03, 41.91) * mm});
            skArc(sketch, "E291", {"start": v(76.03, 41.91) * mm, "mid": v(76.26, 42.07) * mm, "end": v(76.2, 42.34) * mm});
            skLineSegment(sketch, "E292", {"start": v(76.2, 42.34) * mm, "end": v(75.1, 43.44) * mm});
            skArc(sketch, "E293", {"start": v(75.1, 43.44) * mm, "mid": v(74.84, 43.62) * mm, "end": v(74.54, 43.68) * mm});
            skLineSegment(sketch, "E294", {"start": v(74.54, 43.68) * mm, "end": v(69.98, 43.68) * mm});
            skArc(sketch, "E295", {"start": v(69.98, 43.68) * mm, "mid": v(69.01, 43.24) * mm, "end": v(68.58, 42.26) * mm});
            skLineSegment(sketch, "E296", {"start": v(68.58, 42.26) * mm, "end": v(68.58, 37.93) * mm});
            skArc(sketch, "E297", {"start": v(68.58, 37.93) * mm, "mid": v(68.64, 37.63) * mm, "end": v(68.81, 37.37) * mm});
            skLineSegment(sketch, "E298", {"start": v(69.78, 28.3) * mm, "end": v(69.78, 25.3) * mm});
            skArc(sketch, "E299", {"start": v(69.78, 28.3) * mm, "mid": v(69.86, 28.67) * mm, "end": v(70.2, 28.88) * mm});
            skLineSegment(sketch, "E300", {"start": v(73.2, 28.88) * mm, "end": v(70.2, 28.88) * mm});
            skArc(sketch, "E301", {"start": v(73.2, 28.88) * mm, "mid": v(73.64, 28.74) * mm, "end": v(73.78, 28.3) * mm});
            skLineSegment(sketch, "E302", {"start": v(73.78, 25.3) * mm, "end": v(73.78, 28.3) * mm});
            skArc(sketch, "E303", {"start": v(73.78, 25.3) * mm, "mid": v(73.57, 24.96) * mm, "end": v(73.18, 24.88) * mm});
            skLineSegment(sketch, "E304", {"start": v(70.18, 24.88) * mm, "end": v(73.18, 24.88) * mm});
            skArc(sketch, "E305", {"start": v(70.18, 24.88) * mm, "mid": v(69.91, 25.02) * mm, "end": v(69.78, 25.3) * mm});
            skLineSegment(sketch, "E306", {"start": v(87.38, 39.06) * mm, "end": v(87.38, 42.06) * mm});
            skArc(sketch, "E307", {"start": v(87.38, 39.06) * mm, "mid": v(87.3, 38.68) * mm, "end": v(86.97, 38.48) * mm});
            skLineSegment(sketch, "E308", {"start": v(83.97, 38.6) * mm, "end": v(83.97, 38.48) * mm});
            skArc(sketch, "E309", {"start": v(83.97, 38.48) * mm, "mid": v(83.52, 38.61) * mm, "end": v(83.38, 39.06) * mm});
            skLineSegment(sketch, "E310", {"start": v(83.38, 42.06) * mm, "end": v(83.38, 39.06) * mm});
            skArc(sketch, "E311", {"start": v(83.38, 42.06) * mm, "mid": v(83.59, 42.4) * mm, "end": v(83.98, 42.48) * mm});
            skLineSegment(sketch, "E312", {"start": v(86.98, 42.48) * mm, "end": v(83.98, 42.48) * mm});
            skArc(sketch, "E313", {"start": v(86.98, 42.48) * mm, "mid": v(87.25, 42.33) * mm, "end": v(87.38, 42.06) * mm});
            skArc(sketch, "E314", {"start": v(83.97, 28.88) * mm, "mid": v(83.52, 28.74) * mm, "end": v(83.38, 28.3) * mm});
            skLineSegment(sketch, "E315", {"start": v(83.97, 28.88) * mm, "end": v(86.97, 28.88) * mm});
            skArc(sketch, "E316", {"start": v(87.38, 28.3) * mm, "mid": v(87.3, 28.67) * mm, "end": v(86.97, 28.88) * mm});
            skLineSegment(sketch, "E317", {"start": v(87.38, 28.3) * mm, "end": v(87.38, 25.3) * mm});
            skArc(sketch, "E318", {"start": v(86.98, 24.88) * mm, "mid": v(87.25, 25.02) * mm, "end": v(87.38, 25.3) * mm});
            skLineSegment(sketch, "E319", {"start": v(86.98, 24.88) * mm, "end": v(83.98, 24.88) * mm});
            skArc(sketch, "E320", {"start": v(83.38, 25.3) * mm, "mid": v(83.59, 24.96) * mm, "end": v(83.98, 24.88) * mm});
            skLineSegment(sketch, "E321", {"start": v(83.38, 25.3) * mm, "end": v(83.38, 28.3) * mm});
            skCircle(sketch, "E322", {"center": v(78.58, 33.68) * mm, "radius": 2.1 * mm});
            skArc(sketch, "E323", {"start": v(73.2, 38.48) * mm, "mid": v(73.64, 38.61) * mm, "end": v(73.78, 39.06) * mm});
            skLineSegment(sketch, "E324", {"start": v(73.2, 38.48) * mm, "end": v(70.2, 38.48) * mm});
            skArc(sketch, "E325", {"start": v(69.78, 39.06) * mm, "mid": v(69.86, 38.68) * mm, "end": v(70.2, 38.48) * mm});
            skLineSegment(sketch, "E326", {"start": v(69.78, 39.06) * mm, "end": v(69.78, 42.06) * mm});
            skArc(sketch, "E327", {"start": v(70.18, 42.48) * mm, "mid": v(69.91, 42.33) * mm, "end": v(69.78, 42.06) * mm});
            skLineSegment(sketch, "E328", {"start": v(70.18, 42.48) * mm, "end": v(73.18, 42.48) * mm});
            skArc(sketch, "E329", {"start": v(73.78, 42.06) * mm, "mid": v(73.57, 42.4) * mm, "end": v(73.18, 42.48) * mm});
            skLineSegment(sketch, "E330", {"start": v(73.78, 42.06) * mm, "end": v(73.78, 39.06) * mm});
            skLineSegment(sketch, "E331", {"start": v(83.97, 38.48) * mm, "end": v(86.97, 38.48) * mm});
            skLineSegment(sketch, "E332", {"start": v(78.28, 30.24) * mm, "end": v(79.14, 23.68) * mm, "construction": true});
            skLineSegment(sketch, "E333", {"start": v(-3.48, -9.77) * mm, "end": v(3.48, -9.77) * mm});
            skLineSegment(sketch, "E334.0", {"start": v(-1.63, -8.97) * mm, "end": v(0, -8.97) * mm});
            skPoint(sketch, "E335.endSnap0", {"position": v(3.6, -6.63) * mm});
            skPoint(sketch, "E336.orphan", {"position": v(1.35, -9.77) * mm});
            skPoint(sketch, "E337.orphan", {"position": v(-3.6, -7.83) * mm});
            skLineSegment(sketch, "E338", {"start": v(0, -3.18) * mm, "end": v(0, -10.53) * mm, "construction": true});
            skLineSegment(sketch, "E339", {"start": v(-3.28, -8.23) * mm, "end": v(-3.45, -8) * mm});
            skLineSegment(sketch, "E340.MirrorCS", {"start": v(1.63, -8.97) * mm, "end": v(0, -8.97) * mm});
            skLineSegment(sketch, "E341", {"start": v(2.74, -8.23) * mm, "end": v(2.74, -7.46) * mm});
            skPoint(sketch, "E342.orphan", {"position": v(3.45, -8) * mm});
            skPoint(sketch, "E343.MirrorCS.start.orphan", {"position": v(3.28, -8.23) * mm});
            skLineSegment(sketch, "E344", {"start": v(2.74, -7.46) * mm, "end": v(-3.45, -7.44) * mm});
            skLineSegment(sketch, "E345", {"start": v(-3.45, -7.44) * mm, "end": v(-3.45, -8) * mm});
            skLineSegment(sketch, "E346", {"start": v(2.74, -7.46) * mm, "end": v(2.74, -8.23) * mm});
            skPoint(sketch, "E347.orphan", {"position": v(-2.96, -8.23) * mm});
            skLineSegment(sketch, "E348", {"start": v(-9.77, 3.7) * mm, "end": v(-5.7, -0.38) * mm, "construction": true});
            skLineSegment(sketch, "E349", {"start": v(-8.14, 3.6) * mm, "end": v(-8.14, -0.79) * mm, "construction": true});
            skLineSegment(sketch, "E350", {"start": v(-9.77, -3.7) * mm, "end": v(-5.39, 0.7) * mm, "construction": true});
            skLineSegment(sketch, "E351", {"start": v(-8.14, -3.6) * mm, "end": v(-8.14, 0.68) * mm, "construction": true});
            skPoint(sketch, "E352", {"position": v(-8.14, -2.07) * mm});
            skPoint(sketch, "E353", {"position": v(-8.14, 2.07) * mm});
            skLineSegment(sketch, "E354", {"start": v(-10, 6.11) * mm, "end": v(-10, -4.61) * mm, "construction": true});
            skLineSegment(sketch, "E355", {"start": v(-8.93, 2.85) * mm, "end": v(-11.23, 5.16) * mm, "construction": true});
            skLineSegment(sketch, "E356", {"start": v(-8.88, -2.8) * mm, "end": v(-10.64, -4.56) * mm, "construction": true});
            skPoint(sketch, "E357", {"position": v(-10, -3.92) * mm});
            skPoint(sketch, "E358", {"position": v(-10, 3.92) * mm});
            skSolve(sketch);
        }
        {
            var Q0;
            Q0=makeQuery(id+"F0.imprint","IMPRINT",FACE,{"disambiguationData":[TD([[makeQuery(id+"F0.imprint","IMPRINT",EDGE,{"derivedFrom":sQuery(id+"F0.wireOp",EDGE,"E0")}),1.0]])]});
            extrude(context, id + "F1", {"entities" : qUnion([Q0]), "depth" : 340 * mm});
        }
        {
            var Q0;
            Q0=makeQuery(id+"F0.imprint","IMPRINT",FACE,{"disambiguationData":[TD([[makeQuery(id+"F0.imprint","IMPRINT",EDGE,{"derivedFrom":sQuery(id+"F0.wireOp",EDGE,"E111")}),1.0]])]});
            extrude(context, id + "F2", {"entities" : qUnion([Q0]), "depth" : 450 * mm});
        }
        {
            var Q0;
            Q0=makeQuery(id+"F0.imprint","IMPRINT",FACE,{"disambiguationData":[TD([[makeQuery(id+"F0.imprint","IMPRINT",EDGE,{"derivedFrom":sQuery(id+"F0.wireOp",EDGE,"E222")}),1.0]])]});
            extrude(context, id + "F3", {"entities" : qUnion([Q0]), "depth" : 1000 * mm});
        }
        {
            var Q0;
            Q0=makeQuery(id+"F0.imprint","IMPRINT",FACE,{"disambiguationData":[TD([[makeQuery(id+"F0.imprint","IMPRINT",EDGE,{"derivedFrom":sQuery(id+"F0.wireOp",EDGE,"E19")}),1.0]])]});
            extrude(context, id + "F4", {"entities" : qUnion([Q0]), "depth" : 15 * mm});
        }
    });
